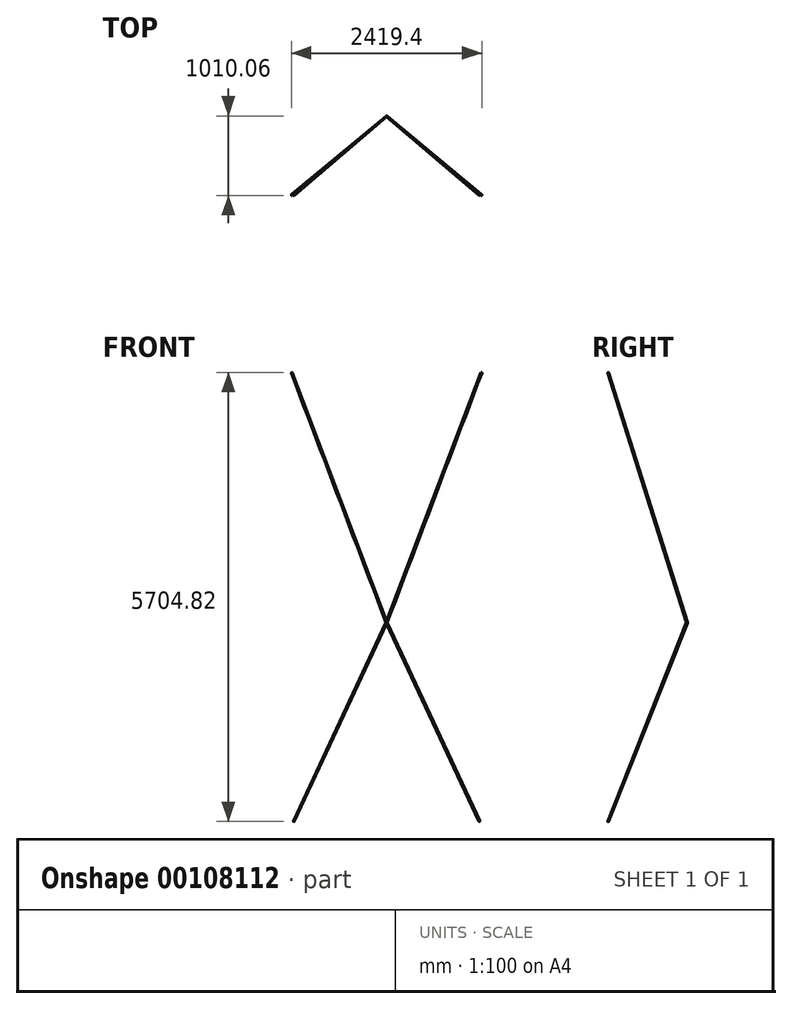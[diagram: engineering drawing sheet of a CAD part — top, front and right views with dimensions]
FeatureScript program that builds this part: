
annotation { "Feature Type Name" : "Feature", "Feature Type Description" : "" }
export const myFeature = defineFeature(function(context is Context, id is Id, definition is map)
    precondition{}
    {
        {
            assignVariable(context, id + "F0", {"name" : "Y1", "anyValue" : 50});
        }
        {
            var Q0;
            Q0=qCreatedBy(makeId("Front.planeOp"),FACE);
            cPlane(context, id + "F1", {"entities" : qUnion([Q0]), "cplaneType" : CPlaneType.OFFSET, "offset" : (getVariable(context, 'Y1')) * mm, "oppositeDirection" : true, "width" : 150 * mm, "height" : 150 * mm});
        }
        {
            var Q0;
            Q0=qCreatedBy(id+"F1.planeOp",FACE);
            var sketch = newSketch(context, id + "F2", { "sketchPlane" : qUnion([Q0])});
            skPoint(sketch, "E0", {"position": v(-1205, 5800) * mm});
            skSolve(sketch);
        }
        {
            assignVariable(context, id + "F3", {"name" : "Y2", "anyValue" : 1050});
        }
        {
            var Q0;
            Q0=qCreatedBy(makeId("Front.planeOp"),FACE);
            cPlane(context, id + "F4", {"entities" : qUnion([Q0]), "cplaneType" : CPlaneType.OFFSET, "offset" : (getVariable(context, 'Y2')) * mm, "oppositeDirection" : true, "width" : 150 * mm, "height" : 150 * mm});
        }
        {
            var Q0;
            Q0=qCreatedBy(id+"F4.planeOp",FACE);
            var sketch = newSketch(context, id + "F5", { "sketchPlane" : qUnion([Q0])});
            skPoint(sketch, "E1", {"position": v(0, 2625) * mm});
            skSolve(sketch);
        }
        {
            assignVariable(context, id + "F6", {"name" : "Y3", "anyValue" : 50});
        }
        {
            var Q0;
            Q0=qCreatedBy(makeId("Front.planeOp"),FACE);
            cPlane(context, id + "F7", {"entities" : qUnion([Q0]), "cplaneType" : CPlaneType.OFFSET, "offset" : (getVariable(context, 'Y3')) * mm, "oppositeDirection" : true, "width" : 150 * mm, "height" : 150 * mm});
        }
        {
            var Q0;
            Q0=qCreatedBy(id+"F7.planeOp",FACE);
            var sketch = newSketch(context, id + "F8", { "sketchPlane" : qUnion([Q0])});
            skPoint(sketch, "E2", {"position": v(1180, 100) * mm});
            skSolve(sketch);
        }
        {
            var Q0;
            Q0=sQuery(id+"F5.wireOp",VERTEX,"E1");
            var Q1;
            Q1=sQuery(id+"F8.wireOp",VERTEX,"E2");
            var Q2;
            Q2=sQuery(id+"F2.wireOp",VERTEX,"E0");
            cPlane(context, id + "F9", {"entities" : qUnion([Q0, Q1, Q2]), "cplaneType" : CPlaneType.THREE_POINT, "offset" : 25 * mm, "width" : 150 * mm, "height" : 150 * mm});
        }
        {
            var Q0;
            Q0=qCreatedBy(id+"F9.planeOp",FACE);
            var sketch = newSketch(context, id + "F10", { "sketchPlane" : qUnion([Q0])});
            skPoint(sketch, "E3.0", {"position": v(-77.9, 5815.63) * mm});
            skPoint(sketch, "E4.0", {"position": v(928.57, 2421.57) * mm});
            skLineSegment(sketch, "E5", {"start": v(-77.9, 5815.63) * mm, "end": v(928.57, 2421.57) * mm});
            skPoint(sketch, "E6.0", {"position": v(-77.9, -363.22) * mm});
            skLineSegment(sketch, "E7", {"start": v(928.57, 2421.57) * mm, "end": v(-77.9, -363.22) * mm});
            skSolve(sketch);
        }
        {
            var Q0;
            Q0=sQuery(id+"F10.wireOp",VERTEX,"E3.0");
            var Q1;
            Q1=sQuery(id+"F10.wireOp",EDGE,"E5");
            cPlane(context, id + "F11", {"entities" : qUnion([Q0, Q1]), "cplaneType" : CPlaneType.LINE_POINT, "offset" : 25 * mm, "width" : 150 * mm, "height" : 150 * mm});
        }
        {
            var Q0;
            Q0=qCreatedBy(id+"F11.planeOp",FACE);
            var sketch = newSketch(context, id + "F12", { "sketchPlane" : qUnion([Q0])});
            skPoint(sketch, "E8.0", {"position": v(744.86, -1790.08) * mm});
            skCircle(sketch, "E9", {"center": v(744.86, -1790.08) * mm, "radius": 5 * mm});
            skSolve(sketch);
        }
        {
            var Q0;
            Q0=makeQuery(id+"F12.imprint","IMPRINT",FACE,{"disambiguationData":[TD([[makeQuery(id+"F12.imprint","IMPRINT",EDGE,{"derivedFrom":sQuery(id+"F12.wireOp",EDGE,"E9")}),1.0]])]});
            var Q1;
            Q1=sQuery(id+"F10.wireOp",EDGE,"E5");
            var Q2;
            Q2=sQuery(id+"F10.wireOp",EDGE,"E7");
            sweep(context, id + "F13", {"profiles" : qUnion([Q0]), "path" : qUnion([Q1, Q2])});
        }
        {
            var Q0;
            Q0=makeQuery(id+"F13.opSweep","SWEPT_BODY",BODY,{"disambiguationData":[OSD([sQuery(id+"F10.wireOp",EDGE,"E7"),sQuery(id+"F12.wireOp",EDGE,"E9")])]});
            var Q1;
            Q1=qCreatedBy(makeId("Right.planeOp"),FACE);
            mirror(context, id + "F14", {"operationType" : NewBodyOperationType.ADD, "entities" : qUnion([Q0]), "mirrorPlane" : qUnion([Q1])});
        }
    });
